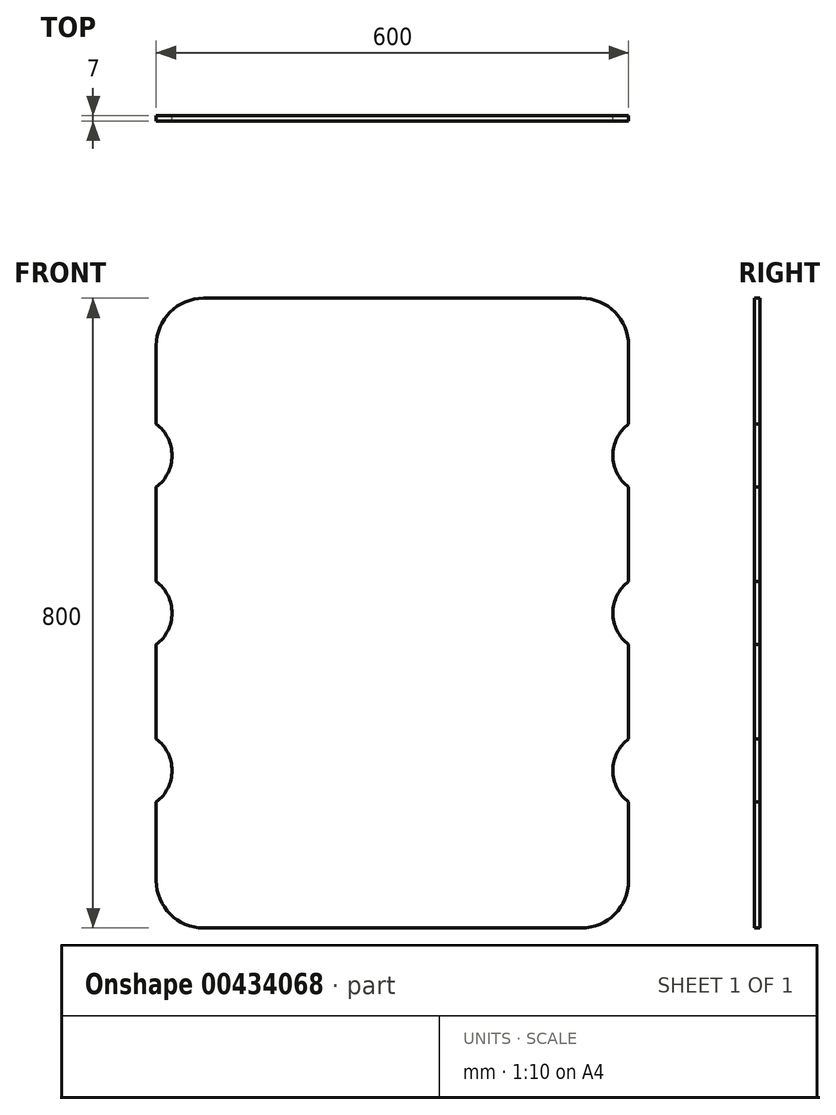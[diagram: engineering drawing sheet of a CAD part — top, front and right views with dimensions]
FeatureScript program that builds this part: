
annotation { "Feature Type Name" : "Feature", "Feature Type Description" : "" }
export const myFeature = defineFeature(function(context is Context, id is Id, definition is map)
    precondition{}
    {
        {
            var Q0;
            Q0=qCreatedBy(makeId("Front.planeOp"),FACE);
            var sketch = newSketch(context, id + "F0", { "sketchPlane" : qUnion([Q0])});
            skLineSegment(sketch, "E0.bottom", {"start": v(0, 0) * mm, "end": v(-300, 0) * mm});
            skLineSegment(sketch, "E0.top", {"start": v(0, 400) * mm, "end": v(-300, 400) * mm});
            skLineSegment(sketch, "E0.left", {"start": v(0, 0) * mm, "end": v(0, 400) * mm});
            skLineSegment(sketch, "E0.right", {"start": v(-300, 0) * mm, "end": v(-300, 400) * mm});
            skCircle(sketch, "E1", {"center": v(-330, 200) * mm, "radius": 50 * mm});
            skCircle(sketch, "E2", {"center": v(-330, 0) * mm, "radius": 50 * mm});
            skSolve(sketch);
        }
        {
            var Q0;
            {var subQ1=sQuery(id+"F0.wireOp",EDGE,"E0.top");Q0=makeQuery(id+"F0.imprint","IMPRINT",FACE,{"disambiguationData":[TD([[makeQuery(id+"F0.imprint","IMPRINT",EDGE,{"derivedFrom":subQ1}),1.0]])]});}
            extrude(context, id + "F1", {"entities" : qUnion([Q0]), "depth" : 7 * mm});
        }
        {
            var Q0;
            Q0=makeQuery(id+"F1.opExtrude","SWEPT_BODY",BODY,{"disambiguationData":[OSD([sQuery(id+"F0.wireOp",EDGE,"E0.bottom"),sQuery(id+"F0.wireOp",EDGE,"E0.top"),sQuery(id+"F0.wireOp",EDGE,"E0.left"),sQuery(id+"F0.wireOp",EDGE,"E0.right")])]});
            var Q1;
            Q1=qCreatedBy(makeId("Right.planeOp"),FACE);
            mirror(context, id + "F2", {"operationType" : NewBodyOperationType.ADD, "entities" : qUnion([Q0]), "mirrorPlane" : qUnion([Q1])});
        }
        {
            var Q0;
            Q0=makeQuery(id+"F1.opExtrude","SWEPT_BODY",BODY,{"disambiguationData":[OSD([sQuery(id+"F0.wireOp",EDGE,"E0.bottom"),sQuery(id+"F0.wireOp",EDGE,"E0.top"),sQuery(id+"F0.wireOp",EDGE,"E0.left"),sQuery(id+"F0.wireOp",EDGE,"E0.right")])]});
            var Q1;
            Q1=qCreatedBy(makeId("Top.planeOp"),FACE);
            mirror(context, id + "F3", {"operationType" : NewBodyOperationType.ADD, "entities" : qUnion([Q0]), "mirrorPlane" : qUnion([Q1])});
        }
        {
            var Q0;
            Q0=makeQuery(id+"F1.opExtrude","SWEPT_EDGE",EDGE,{"disambiguationData":[OSD([sQuery(id+"F0.wireOp",EDGE,"E0.top"),sQuery(id+"F0.wireOp",EDGE,"E0.right")])]});
            var Q1;
            Q1=makeQuery(id+"F2.opPattern","COPY",EDGE,{"derivedFrom":makeQuery(id+"F1.opExtrude","SWEPT_EDGE",EDGE,{"disambiguationData":[OSD([sQuery(id+"F0.wireOp",EDGE,"E0.top"),sQuery(id+"F0.wireOp",EDGE,"E0.right")])]}),"instanceName":"1"});
            var Q2;
            Q2=makeQuery(id+"F3.opPattern","COPY",EDGE,{"derivedFrom":makeQuery(id+"F2.opPattern","COPY",EDGE,{"derivedFrom":makeQuery(id+"F1.opExtrude","SWEPT_EDGE",EDGE,{"disambiguationData":[OSD([sQuery(id+"F0.wireOp",EDGE,"E0.top"),sQuery(id+"F0.wireOp",EDGE,"E0.right")])]}),"instanceName":"1"}),"instanceName":"1"});
            var Q3;
            Q3=makeQuery(id+"F3.opPattern","COPY",EDGE,{"derivedFrom":makeQuery(id+"F1.opExtrude","SWEPT_EDGE",EDGE,{"disambiguationData":[OSD([sQuery(id+"F0.wireOp",EDGE,"E0.top"),sQuery(id+"F0.wireOp",EDGE,"E0.right")])]}),"instanceName":"1"});
            fillet(context, id + "F4", {"entities" : qUnion([Q0, Q1, Q2, Q3]), "radius" : 60 * mm, "tangentPropagation" : true, "allowEdgeOverflow" : false});
        }
    });
